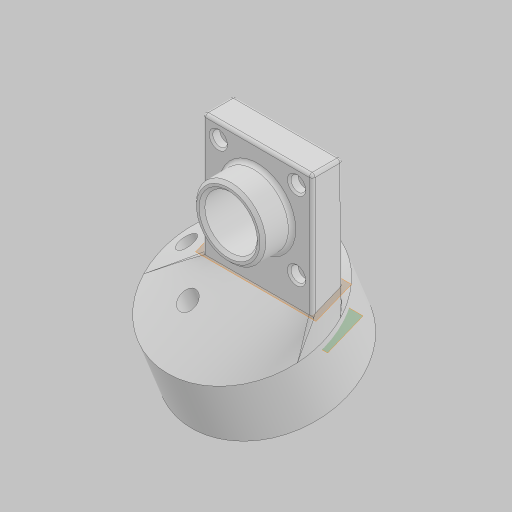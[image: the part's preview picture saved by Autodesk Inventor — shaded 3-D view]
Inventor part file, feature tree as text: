
AUTODESK INVENTOR PART (.ipt)
format: ipt  version: 2023.5 (Build 275446000, 446)  size: 465,920 bytes
history: native  units: in
note: dims shown in document units (in); Inventor stores cm internally (conversion verified against a paired STEP export)
features: extrude x8, hole x3, fillet x3, other x3, projected_geometry x3, plane x2, chamfer x2, sketch x2, loft x1, thicken_offset x1, revolve x1
ambient origin geometry x8: Origin, YZ Plane, XZ Plane, XY Plane, X Axis, Y Axis, Z Axis, Center Point
bodies: Solid1 (feature_tree)
feature tree (29):
  extrude  "Extrusion1"  Depth=0.525in
  extrude  "Extrusion2"  Depth=0.4673in
  plane  "Work Plane1"
  extrude  "Extrusion3"  Depth=1.875in TaperAngle=0.0deg
  loft  "Loft1"
  extrude  "Extrusion4"  Depth=2.75in
  hole  "Hole1"  [1 undecoded]
  extrude  "Extrusion5"  TaperAngle=0.0deg  [1 undecoded]
  extrude  "Extrusion6"  TaperAngle=0.0deg  [1 undecoded]
  hole  "Hole2"  [1 undecoded]
  plane  "Work Plane2"
  fillet  "Fillet1"  Radius=0.3in
  chamfer  "Chamfer1"  Distance=1.1875in
  fillet  "Fillet2"  Radius=0.5in
  extrude  "Extrusion7"  Depth=0.1839in
  fillet  "Fillet3"  Radius=1.3386in
  chamfer  "Chamfer2"  Distance=0.15in
  thicken_offset  "Thicken1"
  hole  "Hole4"  [1 undecoded]
  extrude  "Extrusion8"  Depth=0.9792in
  other  "Edges1"
  other  "Edges2"
  projected_geometry  "Projected Loop1"
  projected_geometry  "Projected Loop2"
  sketch  "Sketch11"  dims[d0=1.875in d1=0.525in]
  other  "Srf1"
  sketch  "Sketch12"  dims[d2=1.875in d3=0.0in d4=0.4673in d5=1.875in d6=0.0in d7=0.6in d9=2.75in d10=0.1in d11=0.0in d12=0.0in d13=90.0deg d14=0.0in d15=90.0deg d16=1.6in d17=0.3in d18=0.0in d19=0.9in d20=0.75in d21=0.119in d22=0.25in d23=0.6871in d24=1.0in d25=0.8108in d26=1.1875in d27=0.5in d28=0.0in d29=0.1839in d30=1.3386in d31=0.15in d32=0.0in d33=0.094in d34=0.75in d35=0.251in d36=0.15in d37=0.6871in d38=1.0in d39=0.8108in d40=0.9792in d41=0.9792in d42=315.0deg d52=0.05in d53=0.05in d54=0.125in d55=45.0deg d56=0.0625in d57=1.0in d58=1.0in d59=0.0in d60=0.25in d61=0.0312in d62=0.125in d63=45.0deg d64=0.2405in d65=90.0deg d66=1.0in d67=1.0in d68=0.177in d69=0.75in d70=0.313in d71=1.45in d72=0.5635in d73=1.0in d74=0.8108in d75=1.25in d76=0.87in d77=1.0in d78=0.0in]
  revolve  "RevolutionSrf1"  Angle=315.0deg
  projected_geometry  "Project Cut Edges1"
note: 5 required parameter values undecoded (feature->parameter linkage not recoverable at this tier; creation-order binding heuristic only, values carry confidence <= 0.55)
